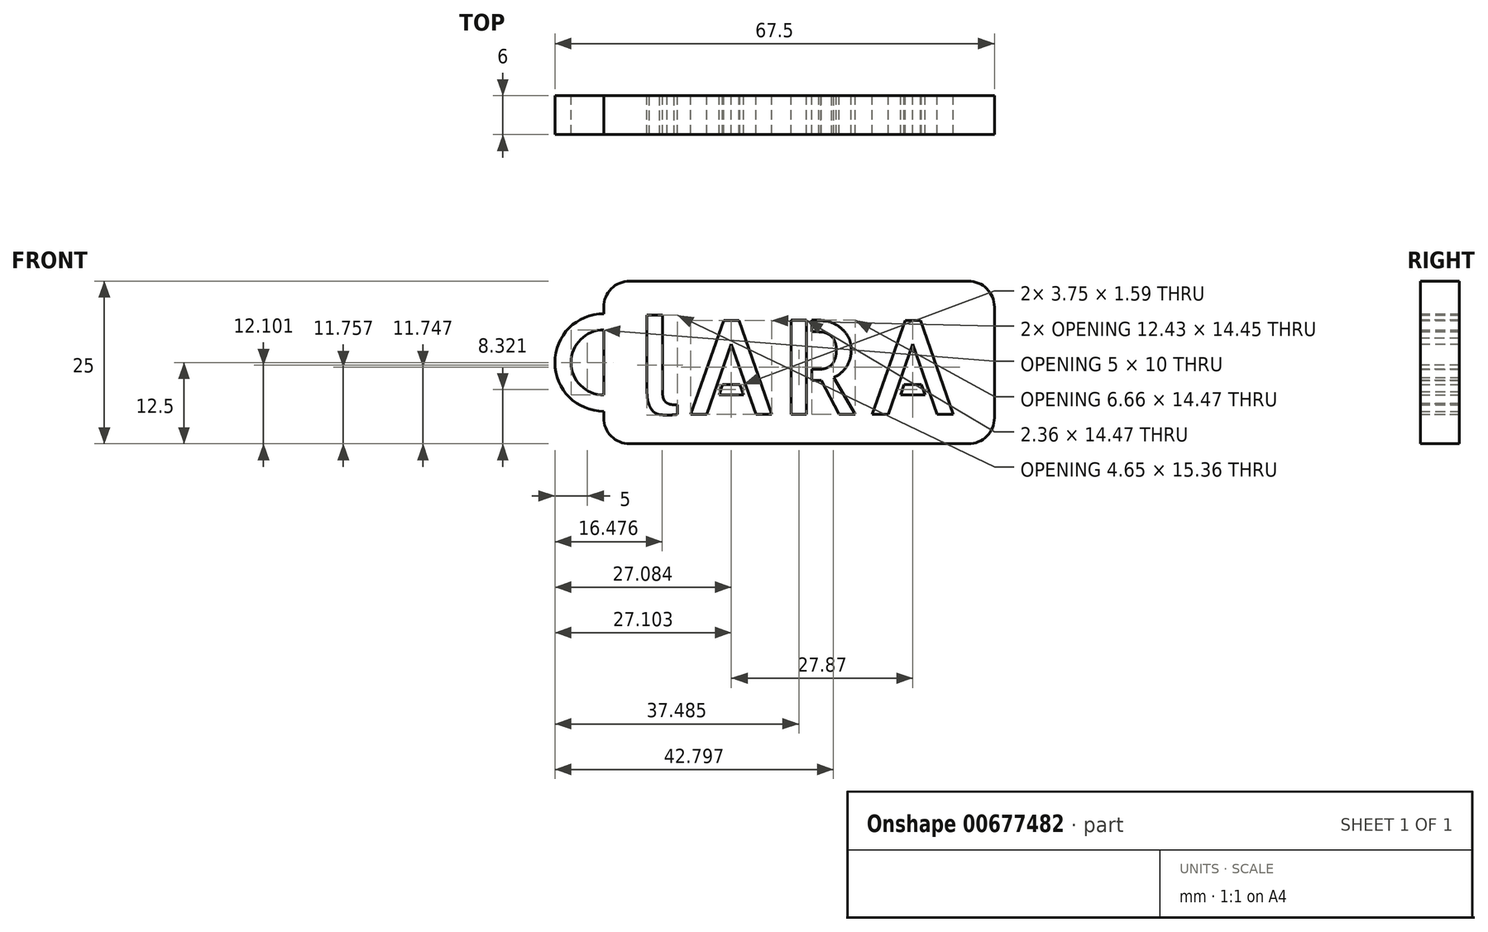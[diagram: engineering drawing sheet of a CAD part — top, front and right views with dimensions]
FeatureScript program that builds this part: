
annotation { "Feature Type Name" : "Feature", "Feature Type Description" : "" }
export const myFeature = defineFeature(function(context is Context, id is Id, definition is map)
    precondition{}
    {
        {
            var Q0;
            Q0=qCreatedBy(makeId("Front.planeOp"),FACE);
            var sketch = newSketch(context, id + "F0", { "sketchPlane" : qUnion([Q0])});
            skLineSegment(sketch, "E0.bottom", {"start": v(-26, 12.5) * mm, "end": v(26, 12.5) * mm});
            skLineSegment(sketch, "E0.top", {"start": v(-26, -12.5) * mm, "end": v(26, -12.5) * mm});
            skLineSegment(sketch, "E0.left", {"start": v(-30, 8.5) * mm, "end": v(-30, -8.5) * mm});
            skLineSegment(sketch, "E0.right", {"start": v(30, 8.5) * mm, "end": v(30, -8.5) * mm});
            skPoint(sketch, "E0.middle", {"position": v(0, 0) * mm});
            skArc(sketch, "E1", {"start": v(-30, 7.5) * mm, "mid": v(-37.5, 0) * mm, "end": v(-30, -7.5) * mm});
            skArc(sketch, "E2", {"start": v(-30, 5) * mm, "mid": v(-35, 0) * mm, "end": v(-30, -5) * mm});
            skText(sketch, "E3", { "text": "lARA", "fontName": "AllertaStencil-Regular.ttf"});
            skPoint(sketch, "E4.visualSharp", {"position": v(-30, 12.5) * mm});
            skArc(sketch, "E4.filletArc", {"start": v(-26, 12.5) * mm, "mid": v(-28.83, 11.33) * mm, "end": v(-30, 8.5) * mm});
            skPoint(sketch, "E5.visualSharp", {"position": v(-30, -12.5) * mm});
            skArc(sketch, "E5.filletArc", {"start": v(-30, -8.5) * mm, "mid": v(-28.83, -11.33) * mm, "end": v(-26, -12.5) * mm});
            skPoint(sketch, "E6.visualSharp", {"position": v(30, -12.5) * mm});
            skArc(sketch, "E6.filletArc", {"start": v(26, -12.5) * mm, "mid": v(28.83, -11.33) * mm, "end": v(30, -8.5) * mm});
            skPoint(sketch, "E7.visualSharp", {"position": v(30, 12.5) * mm});
            skArc(sketch, "E7.filletArc", {"start": v(30, 8.5) * mm, "mid": v(28.83, 11.33) * mm, "end": v(26, 12.5) * mm});
            const initialGuessF0  = {"E3": [-0.025, -0.00798, 1, 0, 0.01448]};
            skSetInitialGuess(sketch, initialGuessF0);
            skSolve(sketch);
        }
        {
            var Q0;
            Q0 = qSketchRegion(id + "F0", true);
            extrude(context, id + "F1", {"entities" : qUnion([Q0]), "depth" : 6 * mm, "offsetDistance" : 25 * mm});
        }
    });
